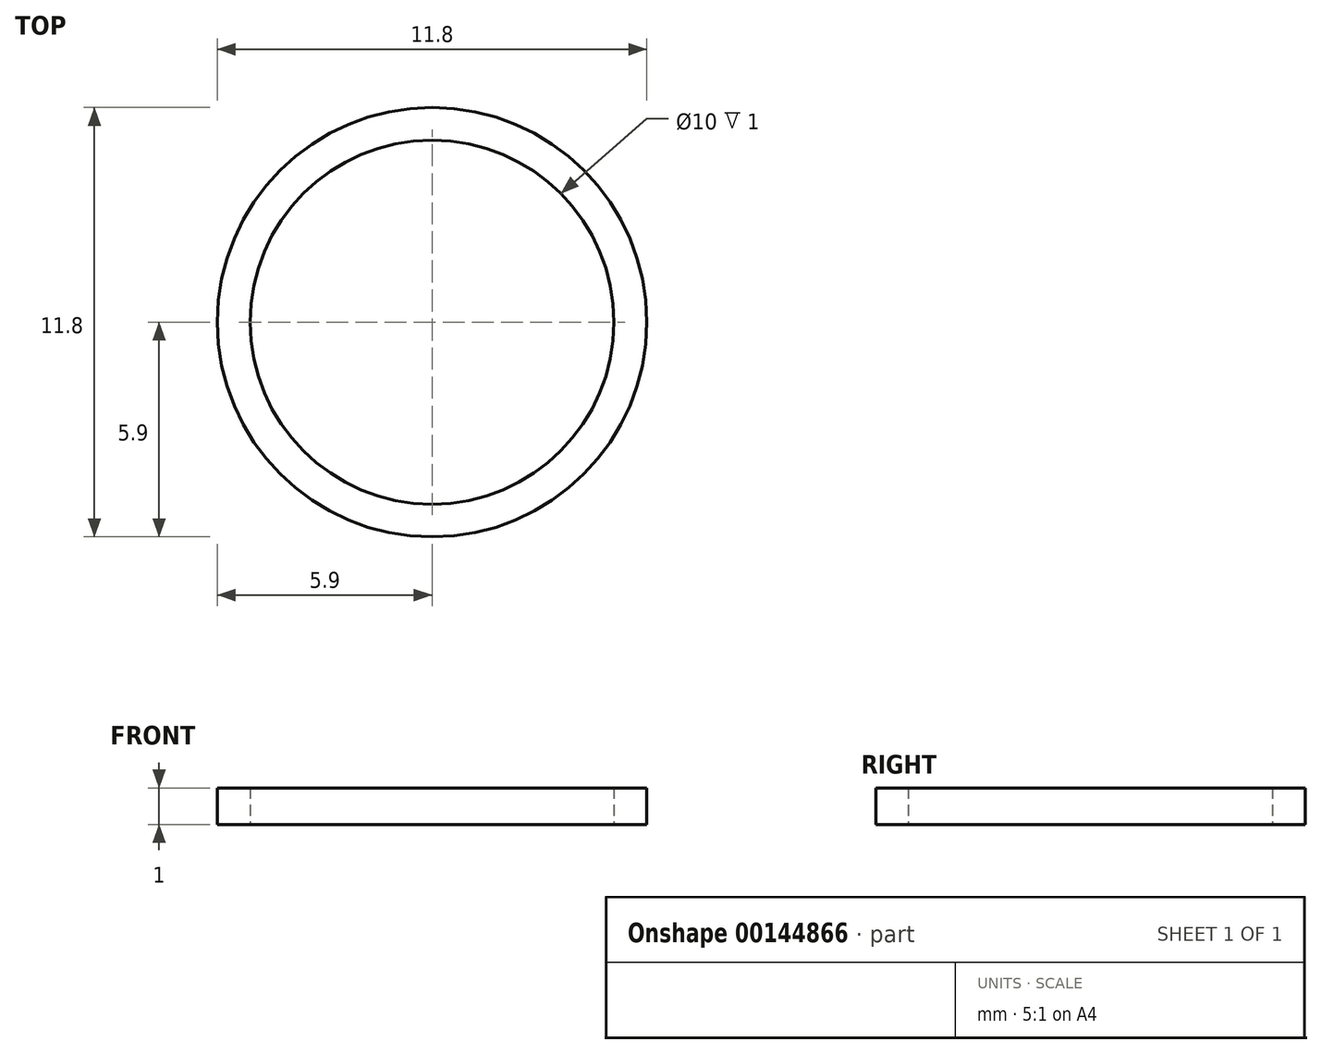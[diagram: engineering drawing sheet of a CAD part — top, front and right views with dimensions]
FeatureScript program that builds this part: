
annotation { "Feature Type Name" : "Feature", "Feature Type Description" : "" }
export const myFeature = defineFeature(function(context is Context, id is Id, definition is map)
    precondition{}
    {
        {
            var Q0;
            Q0=qCreatedBy(makeId("Top.planeOp"),FACE);
            var sketch = newSketch(context, id + "F0", { "sketchPlane" : qUnion([Q0])});
            skCircle(sketch, "E0", {"center": v(0, 0) * mm, "radius": 5 * mm});
            skCircle(sketch, "E1", {"center": v(0, 0) * mm, "radius": 5.9 * mm});
            skSolve(sketch);
        }
        {
            var Q0;
            Q0 = qSketchRegion(id + "F0", true);
            extrude(context, id + "F1", {"entities" : qUnion([Q0]), "depth" : 1 * mm});
        }
    });
